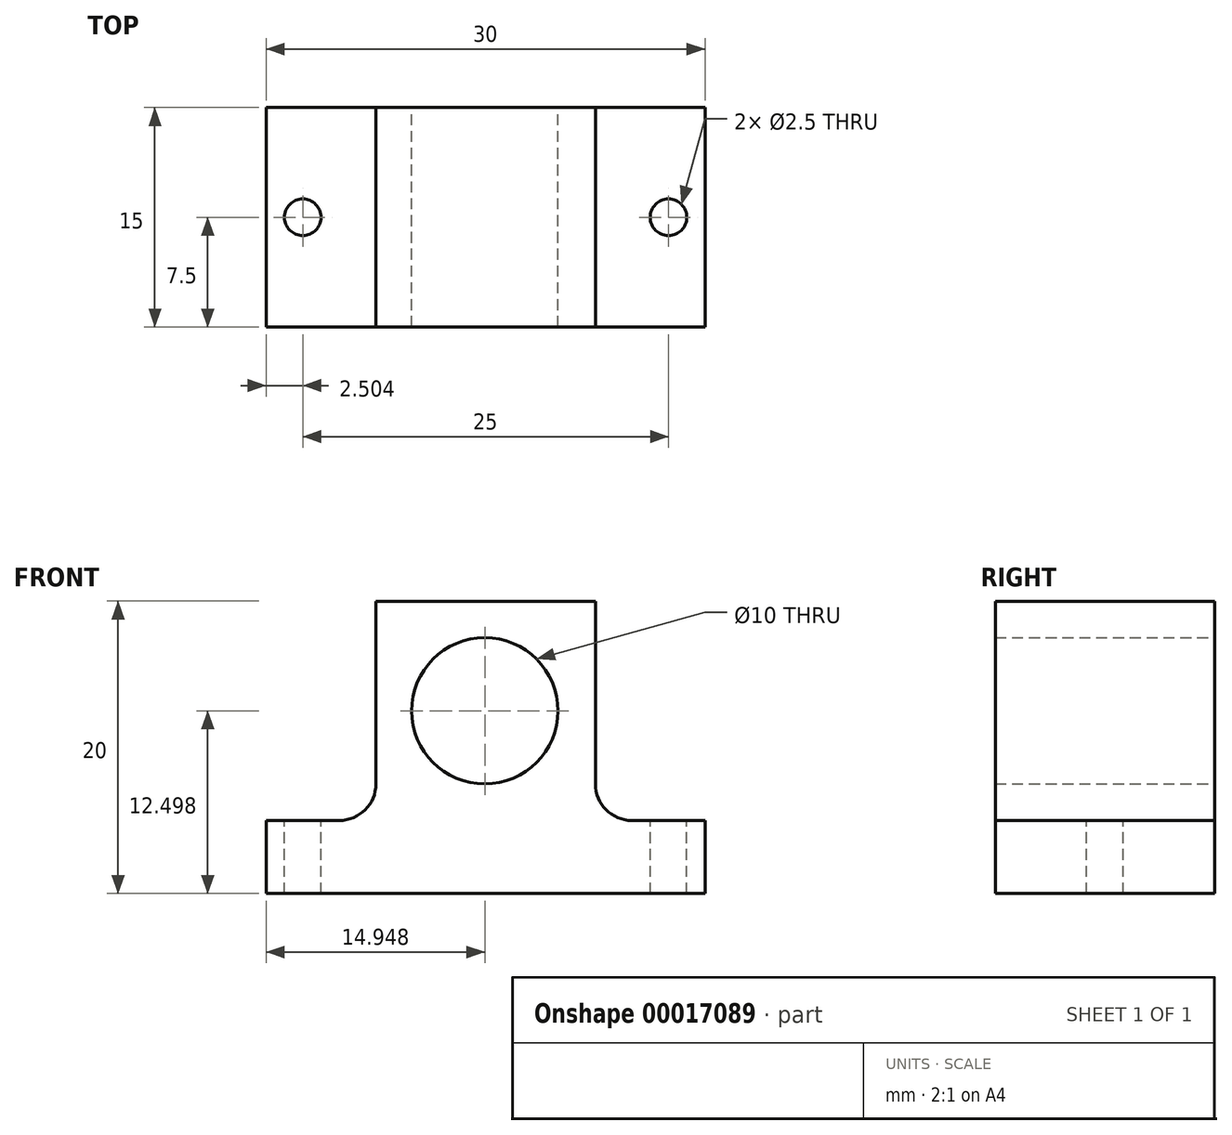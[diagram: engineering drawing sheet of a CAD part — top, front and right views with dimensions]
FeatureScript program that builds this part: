
annotation { "Feature Type Name" : "Feature", "Feature Type Description" : "" }
export const myFeature = defineFeature(function(context is Context, id is Id, definition is map)
    precondition{}
    {
        {
            var Q0;
            Q0=qCreatedBy(makeId("Front.planeOp"),FACE);
            var sketch = newSketch(context, id + "F0", { "sketchPlane" : qUnion([Q0])});
            skLineSegment(sketch, "E0", {"start": v(-30.86, 27.5) * mm, "end": v(-30.86, 22.5) * mm});
            skLineSegment(sketch, "E1", {"start": v(-30.86, 22.5) * mm, "end": v(-0.86, 22.5) * mm});
            skLineSegment(sketch, "E2", {"start": v(-0.86, 22.5) * mm, "end": v(-0.86, 27.5) * mm});
            skLineSegment(sketch, "E3", {"start": v(-0.86, 27.5) * mm, "end": v(-5.86, 27.5) * mm});
            skLineSegment(sketch, "E4", {"start": v(-8.36, 30) * mm, "end": v(-8.36, 42.5) * mm});
            skLineSegment(sketch, "E5", {"start": v(-8.36, 42.5) * mm, "end": v(-23.36, 42.5) * mm});
            skLineSegment(sketch, "E6", {"start": v(-23.36, 42.5) * mm, "end": v(-23.36, 30) * mm});
            skLineSegment(sketch, "E7", {"start": v(-25.86, 27.5) * mm, "end": v(-30.86, 27.5) * mm});
            skPoint(sketch, "E8.visualSharp", {"position": v(-23.36, 27.5) * mm});
            skArc(sketch, "E8.filletArc", {"start": v(-25.86, 27.5) * mm, "mid": v(-24.09, 28.23) * mm, "end": v(-23.36, 30) * mm});
            skPoint(sketch, "E9.visualSharp", {"position": v(-8.36, 27.5) * mm});
            skArc(sketch, "E9.filletArc", {"start": v(-8.36, 30) * mm, "mid": v(-7.62, 28.23) * mm, "end": v(-5.86, 27.5) * mm});
            skCircle(sketch, "E10", {"center": v(-15.91, 35) * mm, "radius": 5 * mm});
            skSolve(sketch);
        }
        {
            var Q0;
            Q0 = qSketchRegion(id + "F0", true);
            extrude(context, id + "F1", {"entities" : qUnion([Q0]), "depth" : 15 * mm});
        }
        {
            var Q0;
            Q0=makeQuery(id+"F1.opExtrude","SWEPT_FACE",FACE,{"disambiguationData":[OSD([sQuery(id+"F0.wireOp",EDGE,"E3")])]});
            var sketch = newSketch(context, id + "F2", { "sketchPlane" : qUnion([Q0])});
            skCircle(sketch, "E11", {"center": v(-3.36, -7.5) * mm, "radius": 1.25 * mm});
            skSolve(sketch);
        }
        {
            var Q0;
            Q0=makeQuery(id+"F2.imprint","IMPRINT",FACE,{"disambiguationData":[TD([[makeQuery(id+"F2.imprint","IMPRINT",EDGE,{"derivedFrom":sQuery(id+"F2.wireOp",EDGE,"E11")}),1.0]])]});
            extrude(context, id + "F3", {"entities" : qUnion([Q0]), "operationType" : NewBodyOperationType.REMOVE, "endBound" : BoundingType.THROUGH_ALL, "oppositeDirection" : true, "depth" : 25 * mm});
        }
        {
            var Q0;
            Q0=makeQuery(id+"F1.opExtrude","SWEPT_FACE",FACE,{"disambiguationData":[OSD([sQuery(id+"F0.wireOp",EDGE,"E7")])]});
            var sketch = newSketch(context, id + "F4", { "sketchPlane" : qUnion([Q0])});
            skCircle(sketch, "E12", {"center": v(-28.36, -7.5) * mm, "radius": 1.25 * mm});
            skSolve(sketch);
        }
        {
            var Q0;
            Q0=makeQuery(id+"F4.imprint","IMPRINT",FACE,{"disambiguationData":[TD([[makeQuery(id+"F4.imprint","IMPRINT",EDGE,{"derivedFrom":sQuery(id+"F4.wireOp",EDGE,"E12")}),1.0]])]});
            extrude(context, id + "F5", {"entities" : qUnion([Q0]), "operationType" : NewBodyOperationType.REMOVE, "endBound" : BoundingType.THROUGH_ALL, "oppositeDirection" : true, "depth" : 25 * mm});
        }
    });
